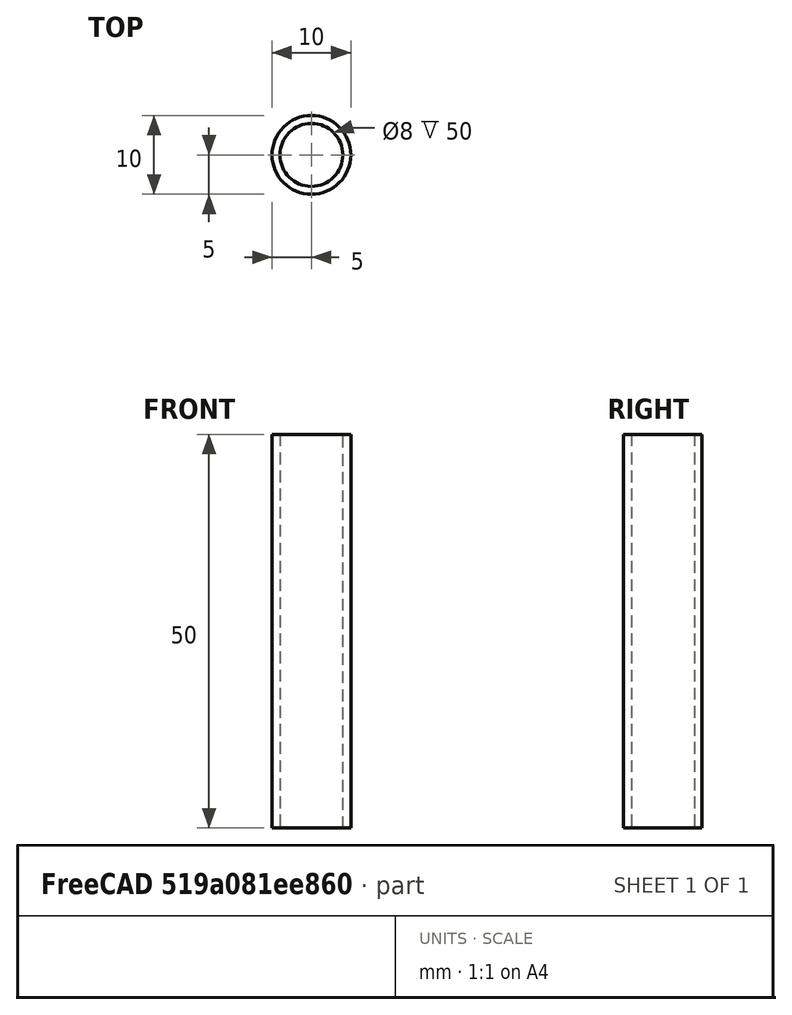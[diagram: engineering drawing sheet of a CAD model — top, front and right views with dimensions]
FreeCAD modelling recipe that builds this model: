
FCSTD DOCUMENT  (FreeCAD 0.19R24276 (Git))
Label: Trubka_40
License: All rights reserved
LicenseURL: http://en.wikipedia.org/wiki/All_rights_reserved
objects: Sketcher::SketchObject×1, PartDesign::Pad×1, PartDesign::Body×1
note: 4 computed .brp shape members not serialized (recipe doc carries the construction recipe); baked Part::Feature solids carry a one-line shape summary decoded from their .brp

FEATURE [Sketcher::SketchObject] Sketch
  FullyConstrained = true
  MapMode = 5
  Support = -> [XY_Plane]
  sketch-geometry (2):
    g0: Circle CenterX=0 CenterY=0 CenterZ=0 NormalX=0 NormalY=0 NormalZ=1 AngleXU=0 Radius=4
    g1: Circle CenterX=0 CenterY=0 CenterZ=0 NormalX=0 NormalY=0 NormalZ=1 AngleXU=0 Radius=5
  constraints (4):
    c: Coincident(g0,g-1)
    c: Coincident(g1,g0)
    c: Diameter(g1) = 10
    c: Diameter(g0) = 8
FEATURE [PartDesign::Pad] Pad
  Direction = (1,1,1)
  Length = 50
  Length2 = 100
  Profile = -> Sketch
  Type = 0
FEATURE [PartDesign::Body] Body
  Group = -> [Sketch,Pad]
  Origin = -> Origin
  Tip = -> Pad
